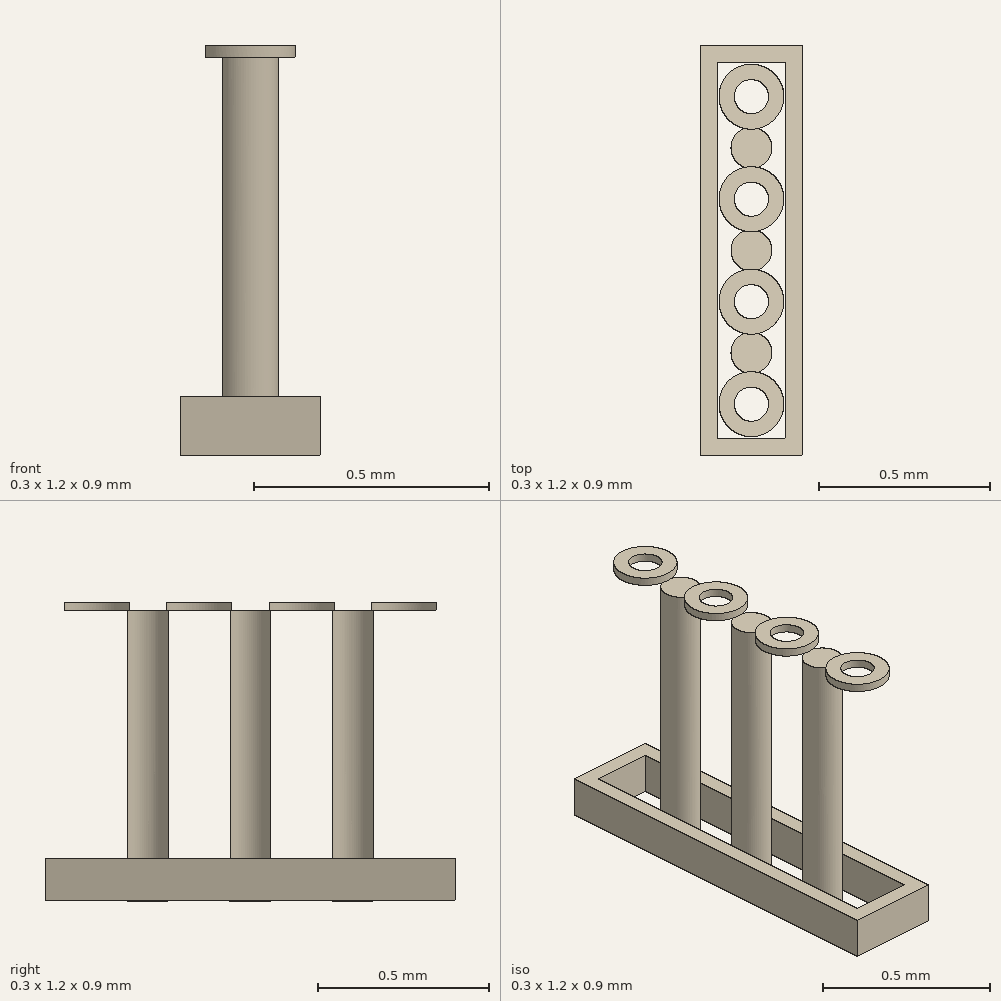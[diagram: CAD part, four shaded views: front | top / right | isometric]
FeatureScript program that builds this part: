
annotation { "Feature Type Name" : "Feature", "Feature Type Description" : "" }
export const myFeature = defineFeature(function(context is Context, id is Id, definition is map)
    precondition{}
    {
        {
            var Q0;
            Q0=qCreatedBy(makeId("Front.planeOp"),FACE);
            var sketch = newSketch(context, id + "F0", { "sketchPlane" : qUnion([Q0])});
            skLineSegment(sketch, "E0.bottom", {"start": v(0, 0) * mm, "end": v(0.3, 0) * mm});
            skLineSegment(sketch, "E0.top", {"start": v(0, 0.12) * mm, "end": v(0.3, 0.12) * mm});
            skLineSegment(sketch, "E0.left", {"start": v(0, 0) * mm, "end": v(0, 0.12) * mm});
            skLineSegment(sketch, "E0.right", {"start": v(0.3, 0) * mm, "end": v(0.3, 0.13) * mm});
            skSolve(sketch);
        }
        {
            var Q0;
            Q0 = qSketchRegion(id + "F0", true);
            var Q1;
            Q1=makeQuery(id+"F0.imprint","IMPRINT",FACE,{"disambiguationData":[TD([[makeQuery(id+"F0.imprint","IMPRINT",EDGE,{"derivedFrom":sQuery(id+"F0.wireOp",EDGE,"E0.bottom")}),1.0]])]});
            extrude(context, id + "F1", {"entities" : qUnion([Q0, Q1]), "depth" : 1.2 * mm});
        }
        {
            var Q0;
            Q0=makeQuery(id+"F1.opExtrude","SWEPT_FACE",FACE,{"disambiguationData":[OSD([sQuery(id+"F0.wireOp",EDGE,"E0.top")])]});
            var sketch = newSketch(context, id + "F2", { "sketchPlane" : qUnion([Q0])});
            skCircle(sketch, "E1", {"center": v(0.15, -0.15) * mm, "radius": 0.1 * mm});
            skCircle(sketch, "E2", {"center": v(0.15, -0.45) * mm, "radius": 0.1 * mm});
            skCircle(sketch, "E3", {"center": v(0.15, -0.75) * mm, "radius": 0.1 * mm});
            skCircle(sketch, "E4", {"center": v(0.15, -1.05) * mm, "radius": 0.1 * mm});
            skSolve(sketch);
        }
        {
            var Q0;
            Q0=makeQuery(id+"F2.imprint","IMPRINT",FACE,{"disambiguationData":[TD([[makeQuery(id+"F2.imprint","IMPRINT",EDGE,{"derivedFrom":sQuery(id+"F2.wireOp",EDGE,"E2")}),1.0]])]});
            var Q1;
            Q1=makeQuery(id+"F2.imprint","IMPRINT",FACE,{"disambiguationData":[TD([[makeQuery(id+"F2.imprint","IMPRINT",EDGE,{"derivedFrom":sQuery(id+"F2.wireOp",EDGE,"E3")}),1.0]])]});
            var Q2;
            Q2=makeQuery(id+"F2.imprint","IMPRINT",FACE,{"disambiguationData":[TD([[makeQuery(id+"F2.imprint","IMPRINT",EDGE,{"derivedFrom":sQuery(id+"F2.wireOp",EDGE,"E4")}),1.0]])]});
            var Q3;
            Q3=makeQuery(id+"F2.imprint","IMPRINT",FACE,{"disambiguationData":[TD([[makeQuery(id+"F2.imprint","IMPRINT",EDGE,{"derivedFrom":sQuery(id+"F2.wireOp",EDGE,"E1")}),1.0]])]});
            extrude(context, id + "F3", {"entities" : qUnion([Q0, Q1, Q2, Q3]), "operationType" : NewBodyOperationType.ADD, "depth" : .75 * mm});
        }
        {
            var Q0;
            Q0=makeQuery(id+"F1.opExtrude","SWEPT_FACE",FACE,{"disambiguationData":[OSD([sQuery(id+"F0.wireOp",EDGE,"E0.bottom")])]});
            var sketch = newSketch(context, id + "F4", { "sketchPlane" : qUnion([Q0])});
            skLineSegment(sketch, "E5.bottom", {"start": v(0.05, 1.15) * mm, "end": v(0.25, 1.15) * mm});
            skLineSegment(sketch, "E5.top", {"start": v(0.05, 0.05) * mm, "end": v(0.25, 0.05) * mm});
            skLineSegment(sketch, "E5.left", {"start": v(0.05, 1.15) * mm, "end": v(0.05, 0.05) * mm});
            skLineSegment(sketch, "E5.right", {"start": v(0.25, 1.15) * mm, "end": v(0.25, 0.05) * mm});
            skSolve(sketch);
        }
        {
            var Q0;
            Q0 = qSketchRegion(id + "F4", true);
            extrude(context, id + "F5", {"entities" : qUnion([Q0]), "operationType" : NewBodyOperationType.REMOVE, "oppositeDirection" : true, "depth" : .85 * mm});
        }
        {
            var Q0;
            Q0=makeQuery(id+"F5.boolean.opBoolean","COPY",FACE,{"derivedFrom":makeQuery(id+"F5.opExtrude","CAP_FACE",FACE,{"disambiguationData":[OSD([sQuery(id+"F4.wireOp",EDGE,"E5.bottom"),sQuery(id+"F4.wireOp",EDGE,"E5.top"),sQuery(id+"F4.wireOp",EDGE,"E5.left"),sQuery(id+"F4.wireOp",EDGE,"E5.right")])],"isStart":false})});
            var sketch = newSketch(context, id + "F6", { "sketchPlane" : qUnion([Q0])});
            skCircle(sketch, "E6", {"center": v(0.15, 1.05) * mm, "radius": 0.05 * mm});
            skCircle(sketch, "E7", {"center": v(0.15, 0.15) * mm, "radius": 0.05 * mm});
            skCircle(sketch, "E8", {"center": v(0.15, 0.75) * mm, "radius": 0.05 * mm});
            skCircle(sketch, "E9", {"center": v(0.15, 0.45) * mm, "radius": 0.05 * mm});
            skSolve(sketch);
        }
        {
            var Q0;
            Q0 = qSketchRegion(id + "F6", true);
            extrude(context, id + "F7", {"entities" : qUnion([Q0]), "operationType" : NewBodyOperationType.REMOVE, "oppositeDirection" : true, "depth" : .1 * mm});
        }
        {
            var Q0;
            Q0=makeQuery(id+"F5.boolean.opBoolean","COPY",FACE,{"derivedFrom":makeQuery(id+"F5.opExtrude","CAP_FACE",FACE,{"disambiguationData":[OSD([sQuery(id+"F4.wireOp",EDGE,"E5.bottom"),sQuery(id+"F4.wireOp",EDGE,"E5.top"),sQuery(id+"F4.wireOp",EDGE,"E5.left"),sQuery(id+"F4.wireOp",EDGE,"E5.right")])],"isStart":false})});
            var sketch = newSketch(context, id + "F8", { "sketchPlane" : qUnion([Q0])});
            skCircle(sketch, "E10", {"center": v(0.15, 0.9) * mm, "radius": 0.06 * mm});
            skCircle(sketch, "E11", {"center": v(0.15, 0.6) * mm, "radius": 0.06 * mm});
            skCircle(sketch, "E12", {"center": v(0.15, 0.3) * mm, "radius": 0.06 * mm});
            skSolve(sketch);
        }
        {
            var Q0;
            Q0 = qSketchRegion(id + "F8", true);
            extrude(context, id + "F9", {"entities" : qUnion([Q0]), "operationType" : NewBodyOperationType.ADD, "depth" : .85 * mm});
        }
    });
